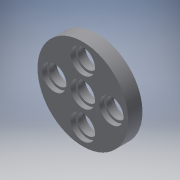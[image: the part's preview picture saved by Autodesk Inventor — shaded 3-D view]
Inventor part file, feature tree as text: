
AUTODESK INVENTOR PART (.ipt)
format: ipt  version: 2017 (Build 210142000, 142)  size: 175,104 bytes
history: native  units: mm
features: extrude x2, sketch x2, plane x1, mirror x1
ambient origin geometry x8: Origin, YZ Plane, XZ Plane, XY Plane, X Axis, Y Axis, Z Axis, Center Point
bodies: Solide1 (feature_tree)
feature tree (6):
  extrude  "Extrusion1"  Depth=1.0mm
  extrude  "Extrusion2"  Depth=6.0mm
  plane  "Work Plane1"
  mirror  "Mirror1"
  sketch  "Esquisse1"
  sketch  "Sketch2"  dims[d0=19.0mm d1=4.1mm d2=20.0mm d4=6.0mm d5=20.0mm d7=6.0mm d10=20.0mm d12=6.0mm d13=20.0mm d15=6.0mm d18=3.0mm d19=0.0mm d20=5.1mm d21=5.1mm d22=5.1mm d23=5.1mm d24=5.1mm d25=1.0mm d26=0.0mm]
